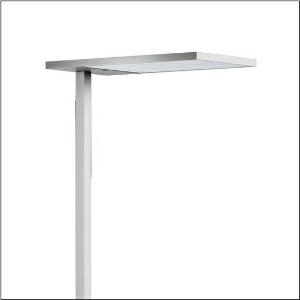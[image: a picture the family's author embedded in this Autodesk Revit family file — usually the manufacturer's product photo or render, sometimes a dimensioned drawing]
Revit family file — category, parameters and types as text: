
# Revit family: silica_r__21_floor_r_51mx53sg4ds_70f9
name_source: partatom
category: Lighting Fixtures
units: mm (PartAtom-declared; Revit-internal decimal feet)

## family parameters
Cut with Voids When Loaded = No
Host = Face
Light Source = No
Part Type = Normal
Room Calculation Point = No
Round Connector Dimension = Use Diameter
Shared = No

## types (1)
- Silica® 21 Floor R (1 x LED, 15000 lm, 106.4 W, 4000K)
    Apparent Load = 106 VA
    CIE Flux Codes = 54 86 97 13 100
    Color Rendering = 80
    Color Temperature = 4000K
    Default Elevation = 1800 mm
    Description = Silica® 21 Floor R, floorstanding luminaire, of PMMA, primary optical cover: prismatic diffuser, of PMMA, CAT 2 (L<= 3000cd/m²), light emission: indirect/direct distribution, primary light characteristic: symmetric, installation type: not mounted, LED, rated luminous flux: 15.000lm, luminous efficacy: 141lm/W, light colour: 840, colour temperature: 4000K, control gear: ECG DALI, daylight-dependent control, mains connection: 230V, 50Hz, connection cable pre-assembled, cable length: 2,5m, rated input power: 106.4W, luminaire head, of aluminium, metallic grey (RAL 9006), length: 650mm, width: 350mm, supporting column, angular, of aluminium, metallic grey (RAL 9006), baseplate, of steel, metallic grey (RAL 9006), protection rating (complete): IP20, insulation class (complete): insulation class I (protective earthing), certification: CE, standard: EN 50419, packaging unit: 1 piece
    Height = 18 mm
    Lamp = 1 x LED
    Lamp Light Flux = 15000 lm
    Lamp Power = 106.4 W
    Lamp count = 1
    Length = 650 mm
    Luminous efficacy = 141 lm/W
    Manufacturer = Siteco
    ModVariant = No
    Model = 51MX53SG4DS
    Mounting Place = Floor
    Mounting Type = Freestanding
    Number of Poles = 1
    OnlyDefault = Yes
    Power Factor = 1
    Product Name = Silica® 21 Floor R
    Product group = floorstanding luminaire
    ProductGroupID = 1302
    Protection Class = Protection class I
    Protection Degree = IP 20
    RLX_Detail_Level = 1
    RlxData = <blob elided: 20153 chars, md5=dd1f79b9>
    Socket = socket
    Standby Power = 0 W
    System Light Flux = 15000 lm
    System Power = 106 W
    Type Comments = Product without accessories
    Type Image = l_1006716.jpg
    URL = http://relux.com
    VarID = ---
    Voltage = 0 V
    Weight = 0.00 kg
    Width = 350 mm

## geometry (parser evidence)
native form markers: Blend x4, Sweep x17
no freeform markers — native parametric forms only
